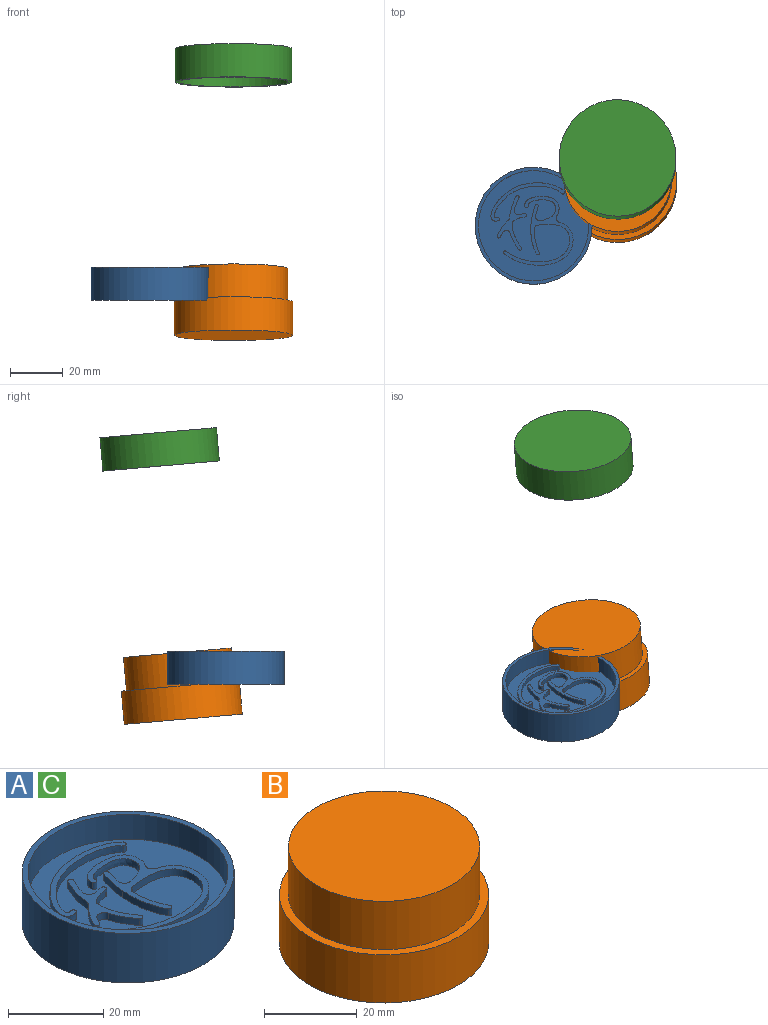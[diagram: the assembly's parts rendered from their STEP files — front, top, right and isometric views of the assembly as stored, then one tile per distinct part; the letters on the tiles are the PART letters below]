
ASSEMBLY  parts=3 mates=1
PART A: 43 faces, bbox 44.5x44.5x12.7 mm
  f0: extruded ~25.64x12.06mm, area 58.7mm2, adj f1,f24,f39,f42
  f1: cylinder r=0.64mm len=1.78mm, axis (0,0,1), area 3.5mm2, adj f0,f13,f39,f42
  f2: extruded ~3.62x1.78mm, area 6.7mm2, adj f18,f27,f39,f40
  f3: extruded ~10.51x8.04mm, area 38mm2, adj f4,f18,f39,f40
  f4: cylinder r=0.64mm len=1.78mm, axis (0,0,1), area 3.5mm2, adj f3,f5,f39,f40
  f5: extruded ~13.04x7.39mm, area 36.4mm2, adj f4,f19,f39,f40
  f6: extruded ~8.75x2.03mm, area 16.1mm2, adj f20,f37,f39,f40
  f7: extruded ~4x1.78mm, area 7.5mm2, adj f14,f38,f39,f41
  f8: extruded ~9.06x3.42mm, area 17.6mm2, adj f14,f31,f39,f41
  f9: extruded ~6.07x3.21mm, area 12.3mm2, adj f15,f31,f39,f41
  f10: extruded ~1.78x1.72mm, area 3.5mm2, adj f15,f32,f39,f41
  f11: extruded ~4.33x1.78mm, area 8.3mm2, adj f17,f35,f39,f41
  f12: extruded ~2x1.78mm, area 3.6mm2, adj f17,f38,f39,f41
  f13: extruded ~27.8x14.59mm, area 68.5mm2, adj f1,f24,f39,f42
  f14: cylinder r=1.59mm len=1.78mm, axis (0,0,1), area 3mm2, adj f7,f8,f39,f41
  f15: cylinder r=1.59mm len=2.89mm, axis (0,0,1), area 6.6mm2, adj f9,f10,f39,f41
  f16: cylinder r=1.59mm len=1.78mm, axis (0,0,1), area 2.1mm2, adj f33,f34,f39,f41
  f17: cylinder r=1.59mm len=2.02mm, axis (0,0,1), area 6mm2, adj f11,f12,f39,f41
  f18: cylinder r=1.59mm len=1.99mm, axis (0,0,1), area 5.8mm2, adj f2,f3,f39,f40
  f19: cylinder r=1.59mm len=2.44mm, axis (0,0,1), area 5.4mm2, adj f5,f28,f39,f40
  f20: cylinder r=1.59mm len=1.78mm, axis (0,0,1), area 3.9mm2, adj f6,f30,f39,f40
  f21: plane 44.45x44.45mm, normal (0,0,1), area 171.5mm2, adj f22,f36
  f22: cylinder r=22.23mm len=44.45mm, axis (0,0,1), area 1773.5mm2, adj f21,f23
  f23: plane 44.45x44.45mm, normal (0,0,-1), area 1551.8mm2, adj f22
  f24: cylinder r=0.64mm len=1.78mm, axis (0,0,1), area 3.5mm2, adj f0,f13,f39,f42
  f25: extruded ~11.29x2.21mm, area 20.7mm2, adj f26,f37,f39,f40
  f26: extruded ~7.21x1.78mm, area 13.1mm2, adj f25,f27,f39,f40
  f27: cylinder r=0.64mm len=1.78mm, axis (0,0,1), area 3.5mm2, adj f2,f26,f39,f40
  f28: extruded ~26.21x16.38mm, area 73.8mm2, adj f19,f29,f39,f40
  f29: cylinder r=0.64mm len=1.78mm, axis (0,0,1), area 3.5mm2, adj f28,f30,f39,f40
  f30: extruded ~24.17x14.33mm, area 80.1mm2, adj f20,f29,f39,f40
  f31: cylinder r=0.64mm len=1.78mm, axis (0,0,1), area 3.5mm2, adj f8,f9,f39,f41
  f32: cylinder r=0.64mm len=1.78mm, axis (0,0,1), area 3.5mm2, adj f10,f33,f39,f41
  f33: extruded ~5.67x4.09mm, area 12.5mm2, adj f16,f32,f39,f41
  f34: extruded ~8.16x2.48mm, area 15.3mm2, adj f16,f35,f39,f41
  f35: cylinder r=0.64mm len=1.78mm, axis (0,0,1), area 3.5mm2, adj f11,f34,f39,f41
  f36: cylinder r=20.96mm len=41.92mm, axis (0,0,1), area 836.3mm2, adj f21,f39
  f37: cylinder r=0.64mm len=1.78mm, axis (0,0,1), area 3.5mm2, adj f6,f25,f39,f40
  f38: cylinder r=0.64mm len=1.78mm, axis (0,0,1), area 3.5mm2, adj f7,f12,f39,f41
  f39: plane 41.92x41.92mm, normal (0,0,1), area 1164.3mm2, adj f0,f1,f2,f3,f4,f5,f6,f7
  f40: plane 26.48x26.24mm, normal (0,0,1), area 120.3mm2, adj f2,f3,f4,f5,f6,f18,f19,f20
  f41: plane 20.77x11.25mm, normal (0,0,1), area 49mm2, adj f7,f8,f9,f10,f11,f12,f14,f15
  f42: plane 28.01x14.63mm, normal (0,0,1), area 46.7mm2, adj f0,f1,f13,f24
PART B: 5 faces, bbox 45x45x25.4 mm
  f0: cylinder r=20.57mm len=41.15mm, axis (0,0,-1), area 1641.7mm2, adj f1,f3
  f1: plane 41.15x41.15mm, normal (0,0,1), area 1329.8mm2, adj f0
  f2: cylinder r=22.52mm len=45.03mm, axis (0,0,-1), area 1796.7mm2, adj f3,f4
  f3: plane 45.03x45.03mm, normal (0,0,1), area 262.8mm2, adj f0,f2
  f4: plane 45.03x45.03mm, normal (0,0,-1), area 1592.6mm2, adj f2
PART C: same geometry as A
PLACE A t=(0,0,-23.37)mm
PLACE B rot(axis=(-0.04,0.04,1),102.2deg) t=(31.93,16.09,-49.3)mm
PLACE C rot(axis=(0.63,0.78,-0.03),176.9deg) t=(31.93,24.51,46.99)mm
MATE slider C.f36 <-> B.f0  axis (0,-0.09,-1) through (31.93,24.79,50.15)mm
